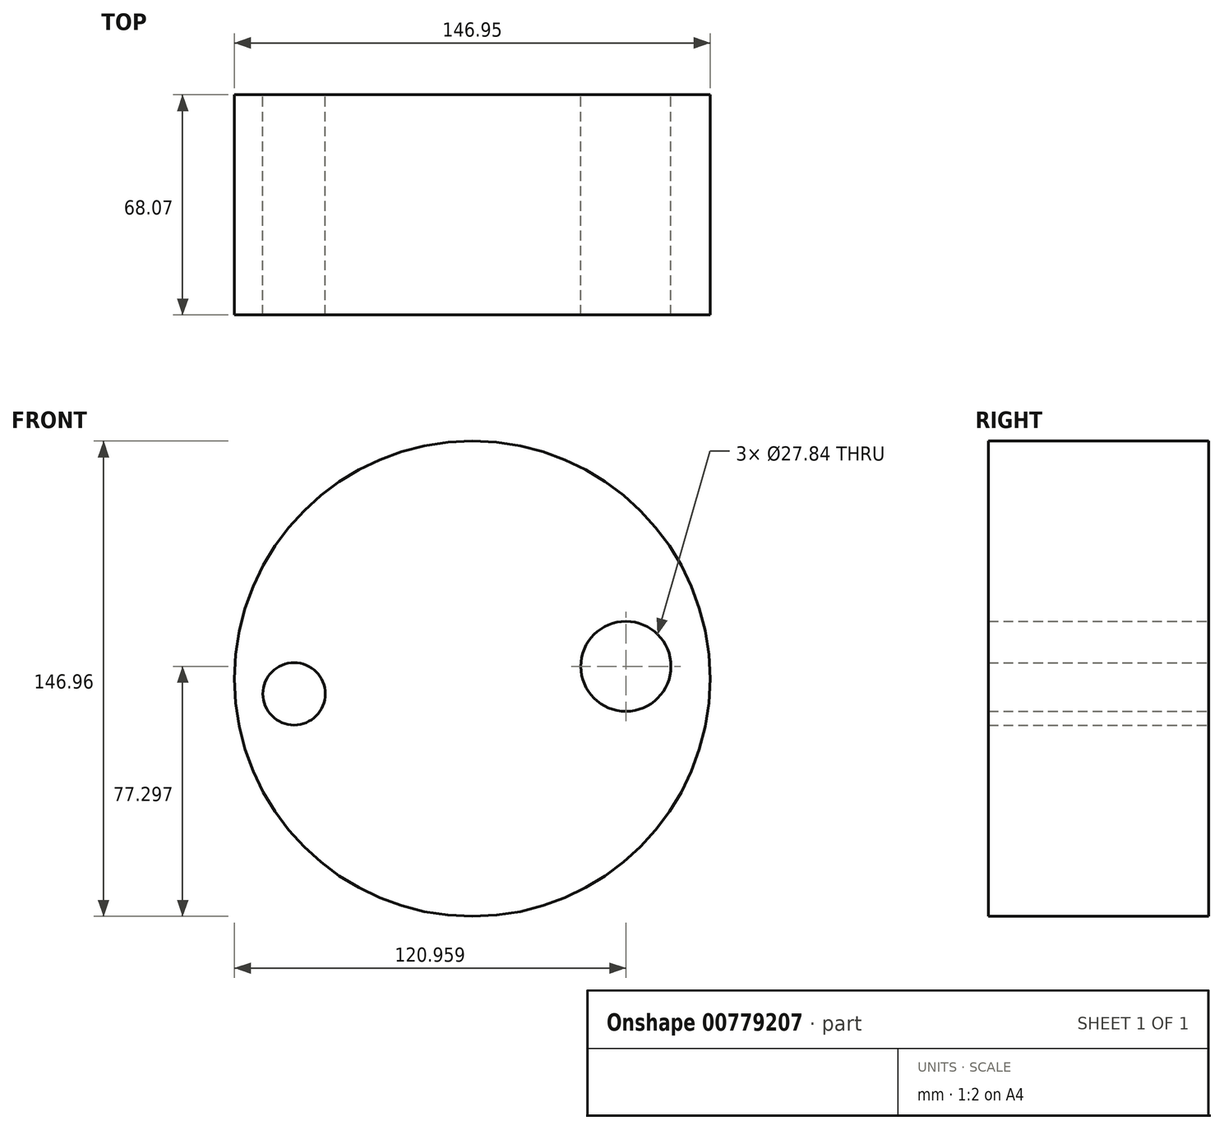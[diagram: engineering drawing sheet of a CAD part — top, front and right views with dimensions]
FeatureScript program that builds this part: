
annotation { "Feature Type Name" : "Feature", "Feature Type Description" : "" }
export const myFeature = defineFeature(function(context is Context, id is Id, definition is map)
    precondition{}
    {
        {
            var Q0;
            Q0=qCreatedBy(makeId("Front.planeOp"),FACE);
            var sketch = newSketch(context, id + "F0", { "sketchPlane" : qUnion([Q0])});
            skCircle(sketch, "E0", {"center": v(14.01, 15.42) * mm, "radius": 73.48 * mm});
            skCircle(sketch, "E1", {"center": v(61.5, 19.24) * mm, "radius": 13.92 * mm});
            skCircle(sketch, "E2", {"center": v(-41.05, 10.74) * mm, "radius": 9.64 * mm});
            skSolve(sketch);
        }
        {
            var Q0;
            Q0=makeQuery(id+"F0.imprint","IMPRINT",FACE,{"disambiguationData":[TD([[makeQuery(id+"F0.imprint","IMPRINT",EDGE,{"derivedFrom":sQuery(id+"F0.wireOp",EDGE,"E0")}),1.0]])]});
            extrude(context, id + "F1", {"entities" : qUnion([Q0]), "depth" : 68.07 * mm, "offsetDistance" : 25.4 * mm});
        }
    });
